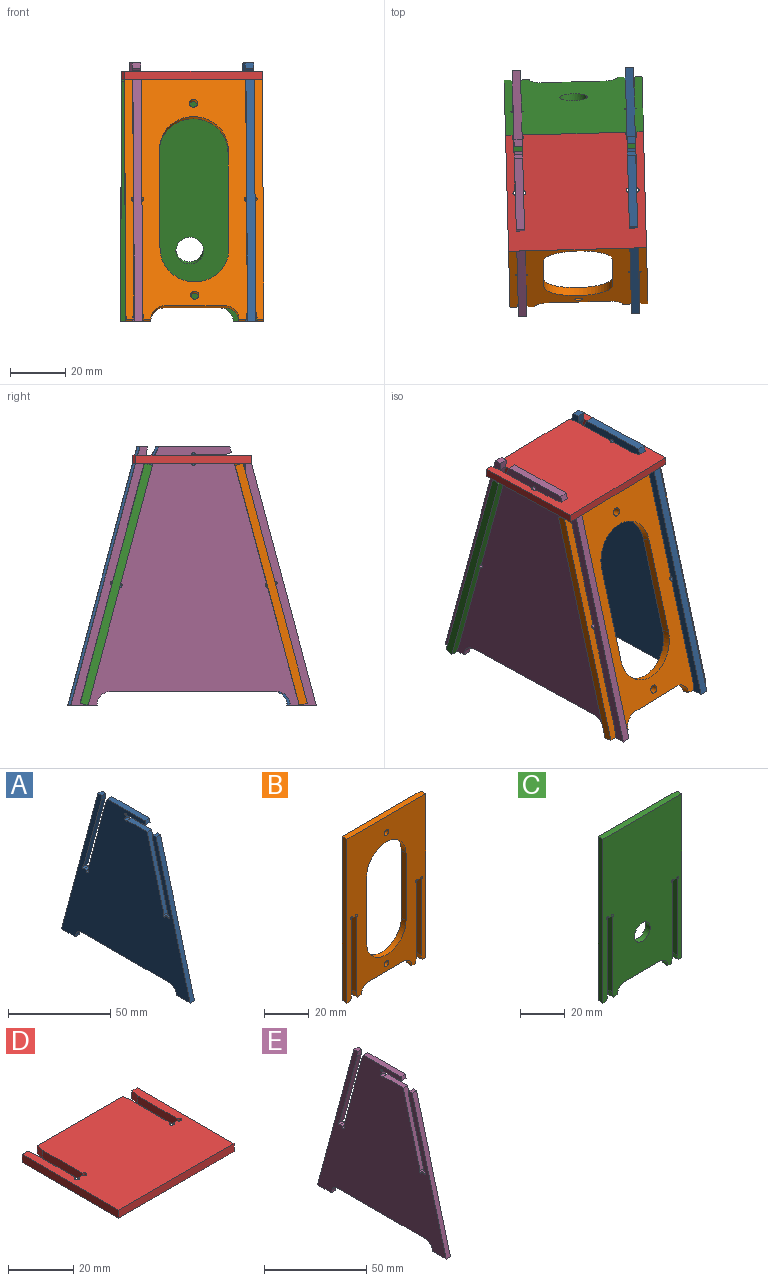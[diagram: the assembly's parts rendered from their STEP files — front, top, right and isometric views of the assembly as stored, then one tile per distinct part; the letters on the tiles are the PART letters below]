
ASSEMBLY  parts=5 mates=13
PART A: 32 faces, bbox 3x89x93.7 mm
  f0: plane 87.71x23.5mm, normal (0,-0.97,0.26), area 272.4mm2, adj f1,f29,f30,f31
  f1: plane 9.49x3mm, normal (0,0,-1), area 28.5mm2, adj f0,f2,f30,f31
  f2: cylinder r=5mm len=5mm, axis (-1,0,0), area 23.6mm2, adj f1,f3,f30,f31
  f3: plane 60.02x3mm, normal (0,0,-1), area 180.1mm2, adj f2,f4,f30,f31
  f4: cylinder r=5mm len=5mm, axis (-1,0,0), area 23.6mm2, adj f3,f5,f30,f31
  f5: plane 9.49x3mm, normal (0,0,-1), area 28.5mm2, adj f4,f6,f30,f31
  f6: plane 93.71x25.11mm, normal (0,0.97,0.26), area 291mm2, adj f5,f7,f30,f31
  f7: plane 3x2.58mm, normal (0,0,1), area 7.7mm2, adj f6,f8,f30,f31
  f8: plane 3x2.9mm, normal (0,-1,-0.09), area 8.7mm2, adj f7,f9,f30,f31
  f9: plane 45.84x12.28mm, normal (0,-0.97,-0.26), area 142.4mm2, adj f8,f10,f30,f31
  f10: cylinder r=0.75mm len=3mm, axis (-1,0,0), area 10.6mm2, adj f9,f11,f30,f31
  f11: plane 3x1.45mm, normal (0,-0.26,0.97), area 4.5mm2, adj f10,f12,f30,f31
  f12: cylinder r=0.75mm len=3mm, axis (-1,0,0), area 10.6mm2, adj f11,f13,f30,f31
  f13: plane 46.62x12.49mm, normal (0,0.97,0.26), area 144.8mm2, adj f12,f14,f30,f31
  f14: plane 3x2.9mm, normal (0,0.91,0.42), area 9.6mm2, adj f13,f15,f30,f31
  f15: plane 25.79x3mm, normal (0,0,1), area 77.4mm2, adj f14,f16,f30,f31
  f16: plane 3x2.15mm, normal (0,-0.97,0.26), area 6.7mm2, adj f15,f17,f30,f31
  f17: plane 3x2.8mm, normal (0,-0.26,-0.97), area 8.7mm2, adj f16,f18,f30,f31
  f18: plane 10.21x3mm, normal (0,0,-1), area 30.6mm2, adj f17,f19,f30,f31
  f19: cylinder r=0.75mm len=3mm, axis (-1,0,0), area 10.6mm2, adj f18,f20,f30,f31
  f20: plane 3x1.6mm, normal (0,-1,0), area 4.8mm2, adj f19,f21,f30,f31
  f21: cylinder r=0.75mm len=3mm, axis (-1,0,0), area 10.6mm2, adj f20,f22,f30,f31
  f22: plane 14.04x3mm, normal (0,0,1), area 42.1mm2, adj f21,f23,f30,f31
  f23: plane 43.52x11.66mm, normal (0,-0.97,0.26), area 135.2mm2, adj f22,f24,f30,f31
  f24: cylinder r=0.75mm len=3mm, axis (-1,0,0), area 10.6mm2, adj f23,f25,f30,f31
  f25: plane 3x1.45mm, normal (0,0.26,0.97), area 4.5mm2, adj f24,f26,f30,f31
  f26: cylinder r=0.75mm len=3mm, axis (-1,0,0), area 10.6mm2, adj f25,f27,f30,f31
  f27: plane 39.74x10.65mm, normal (0,0.97,-0.26), area 123.4mm2, adj f26,f28,f30,f31
  f28: plane 3x3mm, normal (0,1,0), area 9mm2, adj f27,f29,f30,f31
  f29: plane 3x2.3mm, normal (0,0,1), area 6.9mm2, adj f0,f28,f30,f31
  f30: plane 93.71x89.01mm, normal (1,0,0), area 5264mm2, adj f0,f1,f2,f3,f4,f5,f6,f7
  f31: plane 93.71x89.01mm, normal (-1,0,0), area 5264mm2, adj f0,f1,f2,f3,f4,f5,f6,f7
PART B: 32 faces, bbox 50x3x90 mm
  f0: cylinder r=12.5mm len=25mm, axis (0,1,0), area 117.8mm2, adj f1,f29,f30,f31
  f1: plane 37x3mm, normal (-1,0,0), area 111mm2, adj f0,f2,f30,f31
  f2: cylinder r=12.5mm len=25mm, axis (0,1,0), area 117.8mm2, adj f1,f29,f30,f31
  f3: plane 3x2.37mm, normal (0,0,-1), area 7.1mm2, adj f4,f28,f30,f31
  f4: plane 90x3mm, normal (1,0,0), area 270mm2, adj f3,f5,f30,f31
  f5: plane 50x3mm, normal (0,0,1), area 150mm2, adj f4,f6,f30,f31
  f6: plane 90x3mm, normal (-1,0,0), area 270mm2, adj f5,f7,f30,f31
  f7: plane 3x2.37mm, normal (0,0,-1), area 7.1mm2, adj f6,f8,f30,f31
  f8: plane 3x3mm, normal (0.98,0,-0.17), area 9.1mm2, adj f7,f9,f30,f31
  f9: plane 41.25x3mm, normal (1,0,0), area 123.8mm2, adj f8,f10,f30,f31
  f10: cylinder r=0.75mm len=3mm, axis (0,1,0), area 10.6mm2, adj f9,f11,f30,f31
  f11: plane 3x1.6mm, normal (0,0,-1), area 4.8mm2, adj f10,f12,f30,f31
  f12: cylinder r=0.75mm len=3mm, axis (0,1,0), area 10.6mm2, adj f11,f13,f30,f31
  f13: plane 41.25x3mm, normal (-1,0,0), area 123.8mm2, adj f12,f14,f30,f31
  f14: plane 3x3mm, normal (-0.98,0,-0.17), area 9.1mm2, adj f13,f15,f30,f31
  f15: plane 3x2.47mm, normal (0,0,-1), area 7.4mm2, adj f14,f16,f30,f31
  f16: cylinder r=5mm len=5mm, axis (0,1,0), area 23.6mm2, adj f15,f17,f30,f31
  f17: plane 22x3mm, normal (0,0,-1), area 66mm2, adj f16,f18,f30,f31
  f18: cylinder r=5mm len=5mm, axis (0,1,0), area 23.6mm2, adj f17,f19,f30,f31
  f19: plane 3x2.47mm, normal (0,0,-1), area 7.4mm2, adj f18,f20,f30,f31
  f20: plane 3x3mm, normal (0.98,0,-0.17), area 9.1mm2, adj f19,f21,f30,f31
  f21: plane 41.25x3mm, normal (1,0,0), area 123.8mm2, adj f20,f22,f30,f31
  f22: cylinder r=0.75mm len=3mm, axis (0,1,0), area 10.6mm2, adj f21,f23,f30,f31
  f23: plane 3x1.6mm, normal (0,0,-1), area 4.8mm2, adj f22,f24,f30,f31
  f24: cylinder r=0.75mm len=3mm, axis (0,1,0), area 10.6mm2, adj f23,f25,f30,f31
  f25: plane 41.25x3mm, normal (-1,0,0), area 123.8mm2, adj f24,f28,f30,f31
  f26: cylinder r=1.5mm len=3mm, axis (0,1,0), area 28.3mm2, adj f30,f31
  f27: cylinder r=1.5mm len=3mm, axis (0,1,0), area 28.3mm2, adj f30,f31
  f28: plane 3x3mm, normal (-0.98,0,-0.17), area 9.1mm2, adj f3,f25,f30,f31
  f29: plane 37x3mm, normal (1,0,0), area 111mm2, adj f0,f2,f30,f31
  f30: plane 90x50mm, normal (0,-1,0), area 2633.2mm2, adj f0,f1,f2,f3,f4,f5,f6,f7
  f31: plane 90x50mm, normal (0,1,0), area 2633.2mm2, adj f0,f1,f2,f3,f4,f5,f6,f7
PART C: 27 faces, bbox 50x3x90 mm
  f0: plane 3x2.37mm, normal (0,0,-1), area 7.1mm2, adj f1,f23,f25,f26
  f1: plane 90x3mm, normal (1,0,0), area 270mm2, adj f0,f2,f25,f26
  f2: plane 50x3mm, normal (0,0,1), area 150mm2, adj f1,f3,f25,f26
  f3: plane 90x3mm, normal (-1,0,0), area 270mm2, adj f2,f4,f25,f26
  f4: plane 3x2.37mm, normal (0,0,-1), area 7.1mm2, adj f3,f5,f25,f26
  f5: plane 3x3mm, normal (0.98,0,-0.17), area 9.1mm2, adj f4,f6,f25,f26
  f6: plane 41.25x3mm, normal (1,0,0), area 123.8mm2, adj f5,f7,f25,f26
  f7: cylinder r=0.75mm len=3mm, axis (0,-1,0), area 10.6mm2, adj f6,f8,f25,f26
  f8: plane 3x1.6mm, normal (0,0,-1), area 4.8mm2, adj f7,f9,f25,f26
  f9: cylinder r=0.75mm len=3mm, axis (0,-1,0), area 10.6mm2, adj f8,f10,f25,f26
  f10: plane 41.25x3mm, normal (-1,0,0), area 123.8mm2, adj f9,f11,f25,f26
  f11: plane 3x3mm, normal (-0.98,0,-0.17), area 9.1mm2, adj f10,f12,f25,f26
  f12: plane 3x2.47mm, normal (0,0,-1), area 7.4mm2, adj f11,f13,f25,f26
  f13: cylinder r=5mm len=5mm, axis (0,-1,0), area 23.6mm2, adj f12,f14,f25,f26
  f14: plane 22x3mm, normal (0,0,-1), area 66mm2, adj f13,f15,f25,f26
  f15: cylinder r=5mm len=5mm, axis (0,-1,0), area 23.6mm2, adj f14,f16,f25,f26
  f16: plane 3x2.47mm, normal (0,0,-1), area 7.4mm2, adj f15,f17,f25,f26
  f17: plane 3x3mm, normal (0.98,0,-0.17), area 9.1mm2, adj f16,f18,f25,f26
  f18: plane 41.25x3mm, normal (1,0,0), area 123.8mm2, adj f17,f19,f25,f26
  f19: cylinder r=0.75mm len=3mm, axis (0,-1,0), area 10.6mm2, adj f18,f20,f25,f26
  f20: plane 3x1.6mm, normal (0,0,-1), area 4.8mm2, adj f19,f21,f25,f26
  f21: cylinder r=0.75mm len=3mm, axis (0,-1,0), area 10.6mm2, adj f20,f22,f25,f26
  f22: plane 41.25x3mm, normal (-1,0,0), area 123.8mm2, adj f21,f23,f25,f26
  f23: plane 3x3mm, normal (-0.98,0,-0.17), area 9.1mm2, adj f0,f22,f25,f26
  f24: cylinder r=5mm len=10mm, axis (0,-1,0), area 94.2mm2, adj f25,f26
  f25: plane 90x50mm, normal (0,1,0), area 3984.7mm2, adj f0,f1,f2,f3,f4,f5,f6,f7
  f26: plane 90x50mm, normal (0,-1,0), area 3984.7mm2, adj f0,f1,f2,f3,f4,f5,f6,f7
PART D: 22 faces, bbox 50x42x3 mm
  f0: plane 42x3mm, normal (1,0,0), area 126mm2, adj f1,f19,f20,f21
  f1: plane 3x2.37mm, normal (0,1,0), area 7.1mm2, adj f0,f2,f20,f21
  f2: plane 3x3mm, normal (-0.98,0.17,0), area 9.1mm2, adj f1,f3,f20,f21
  f3: plane 17.25x3mm, normal (-1,0,0), area 51.8mm2, adj f2,f4,f20,f21
  f4: cylinder r=0.75mm len=3mm, axis (0,0,-1), area 10.6mm2, adj f3,f5,f20,f21
  f5: plane 3x1.6mm, normal (0,1,0), area 4.8mm2, adj f4,f6,f20,f21
  f6: cylinder r=0.75mm len=3mm, axis (0,0,-1), area 10.6mm2, adj f5,f7,f20,f21
  f7: plane 17.25x3mm, normal (1,0,0), area 51.8mm2, adj f6,f8,f20,f21
  f8: plane 3x3mm, normal (0.98,0.17,0), area 9.1mm2, adj f7,f9,f20,f21
  f9: plane 36.94x3mm, normal (0,1,0), area 110.8mm2, adj f8,f10,f20,f21
  f10: plane 3x3mm, normal (-0.98,0.17,0), area 9.1mm2, adj f9,f11,f20,f21
  f11: plane 17.25x3mm, normal (-1,0,0), area 51.8mm2, adj f10,f12,f20,f21
  f12: cylinder r=0.75mm len=3mm, axis (0,0,-1), area 10.6mm2, adj f11,f13,f20,f21
  f13: plane 3x1.6mm, normal (0,1,0), area 4.8mm2, adj f12,f14,f20,f21
  f14: cylinder r=0.75mm len=3mm, axis (0,0,-1), area 10.6mm2, adj f13,f15,f20,f21
  f15: plane 17.25x3mm, normal (1,0,0), area 51.8mm2, adj f14,f16,f20,f21
  f16: plane 3x3mm, normal (0.98,0.17,0), area 9.1mm2, adj f15,f17,f20,f21
  f17: plane 3x2.37mm, normal (0,1,0), area 7.1mm2, adj f16,f18,f20,f21
  f18: plane 42x3mm, normal (-1,0,0), area 126mm2, adj f17,f19,f20,f21
  f19: plane 50x3mm, normal (0,-1,0), area 150mm2, adj f0,f18,f20,f21
  f20: plane 50x42mm, normal (0,0,1), area 1961.3mm2, adj f0,f1,f2,f3,f4,f5,f6,f7
  f21: plane 50x42mm, normal (0,0,-1), area 1961.3mm2, adj f0,f1,f2,f3,f4,f5,f6,f7
PART E: 32 faces, bbox 3x89x93.7 mm
  f0: plane 87.71x23.5mm, normal (0,-0.97,0.26), area 272.4mm2, adj f1,f29,f30,f31
  f1: plane 9.49x3mm, normal (0,0,-1), area 28.5mm2, adj f0,f2,f30,f31
  f2: cylinder r=5mm len=5mm, axis (1,0,0), area 23.6mm2, adj f1,f3,f30,f31
  f3: plane 60.02x3mm, normal (0,0,-1), area 180.1mm2, adj f2,f4,f30,f31
  f4: cylinder r=5mm len=5mm, axis (1,0,0), area 23.6mm2, adj f3,f5,f30,f31
  f5: plane 9.49x3mm, normal (0,0,-1), area 28.5mm2, adj f4,f6,f30,f31
  f6: plane 93.71x25.11mm, normal (0,0.97,0.26), area 291mm2, adj f5,f7,f30,f31
  f7: plane 3x2.58mm, normal (0,0,1), area 7.7mm2, adj f6,f8,f30,f31
  f8: plane 3x2.9mm, normal (0,-1,-0.09), area 8.7mm2, adj f7,f9,f30,f31
  f9: plane 45.84x12.28mm, normal (0,-0.97,-0.26), area 142.4mm2, adj f8,f10,f30,f31
  f10: cylinder r=0.75mm len=3mm, axis (1,0,0), area 10.6mm2, adj f9,f11,f30,f31
  f11: plane 3x1.45mm, normal (0,-0.26,0.97), area 4.5mm2, adj f10,f12,f30,f31
  f12: cylinder r=0.75mm len=3mm, axis (1,0,0), area 10.6mm2, adj f11,f13,f30,f31
  f13: plane 46.62x12.49mm, normal (0,0.97,0.26), area 144.8mm2, adj f12,f14,f30,f31
  f14: plane 3x2.9mm, normal (0,0.91,0.42), area 9.6mm2, adj f13,f15,f30,f31
  f15: plane 25.79x3mm, normal (0,0,1), area 77.4mm2, adj f14,f16,f30,f31
  f16: plane 3x2.15mm, normal (0,-0.97,0.26), area 6.7mm2, adj f15,f17,f30,f31
  f17: plane 3x2.8mm, normal (0,-0.26,-0.97), area 8.7mm2, adj f16,f18,f30,f31
  f18: plane 10.21x3mm, normal (0,0,-1), area 30.6mm2, adj f17,f19,f30,f31
  f19: cylinder r=0.75mm len=3mm, axis (1,0,0), area 10.6mm2, adj f18,f20,f30,f31
  f20: plane 3x1.6mm, normal (0,-1,0), area 4.8mm2, adj f19,f21,f30,f31
  f21: cylinder r=0.75mm len=3mm, axis (1,0,0), area 10.6mm2, adj f20,f22,f30,f31
  f22: plane 14.04x3mm, normal (0,0,1), area 42.1mm2, adj f21,f23,f30,f31
  f23: plane 43.52x11.66mm, normal (0,-0.97,0.26), area 135.2mm2, adj f22,f24,f30,f31
  f24: cylinder r=0.75mm len=3mm, axis (1,0,0), area 10.6mm2, adj f23,f25,f30,f31
  f25: plane 3x1.45mm, normal (0,0.26,0.97), area 4.5mm2, adj f24,f26,f30,f31
  f26: cylinder r=0.75mm len=3mm, axis (1,0,0), area 10.6mm2, adj f25,f27,f30,f31
  f27: plane 39.74x10.65mm, normal (0,0.97,-0.26), area 123.4mm2, adj f26,f28,f30,f31
  f28: plane 3x3mm, normal (0,1,0), area 9mm2, adj f27,f29,f30,f31
  f29: plane 3x2.3mm, normal (0,0,1), area 6.9mm2, adj f0,f28,f30,f31
  f30: plane 93.71x89.01mm, normal (-1,0,0), area 5264mm2, adj f0,f1,f2,f3,f4,f5,f6,f7
  f31: plane 93.71x89.01mm, normal (1,0,0), area 5264mm2, adj f0,f1,f2,f3,f4,f5,f6,f7
PLACE A rot(axis=(0,0,1),1.5deg) t=(-25.65,-41.05,-23.45)mm
PLACE B rot(axis=(-1,-0.01,0.1),15.1deg) t=(-43.95,-68.18,-23.45)mm
PLACE C rot(axis=(1,0.01,0.1),15.1deg) t=(-45.34,-14.9,-23.45)mm
PLACE D rot(axis=(0,0,1),1.5deg) t=(-44.64,-41.54,20.8)mm
PLACE E rot(axis=(0,0,1),1.5deg) t=(-63.64,-42.04,-23.45)mm fixed
MATE planar A.f20 <-> D.f5  axis (0.03,-1,0) through (-25.65,-41.05,22.35)mm
MATE planar B.f23 <-> A.f25  axis (0.01,-0.26,-0.97) through (-23.36,-69.09,-23.06)mm
MATE planar A.f24 <-> B.f21  axis (-1,-0.03,0) through (-24.95,-67.68,-23.45)mm
MATE planar E.f23 <-> B.f31  axis (0.03,-0.97,0.26) through (-64.6,-62.69,-0.96)mm
MATE planar C.f18 <-> A.f31  axis (1,0.03,0) through (-26.53,-7.43,-43.71)mm
MATE planar B.f30 <-> A.f27  axis (0.03,-0.97,0.26) through (-31.5,-65.96,-4.8)mm
MATE planar A.f11 <-> C.f20  axis (0.01,-0.26,0.97) through (-23.39,-12.88,-23.06)mm
MATE planar A.f31 <-> D.f7  axis (-1,-0.03,0) through (-26.01,-27.09,23.9)mm
MATE planar C.f26 <-> A.f13  axis (0.03,-0.97,-0.26) through (-45.32,-15.83,-20)mm
MATE planar B.f11 <-> E.f25  axis (0.01,-0.26,-0.97) through (-64.45,-70.17,-23.06)mm
MATE parallel E.f31 <-> A.f31  axis (1,0.03,0) through (-63.64,-41.91,-26.03)mm
MATE planar D.f21 <-> A.f22  axis (0,0,-1) through (-45.19,-20.55,20.8)mm
MATE planar E.f31 <-> B.f13  axis (1,0.03,0) through (-63.64,-41.91,-26.03)mm
